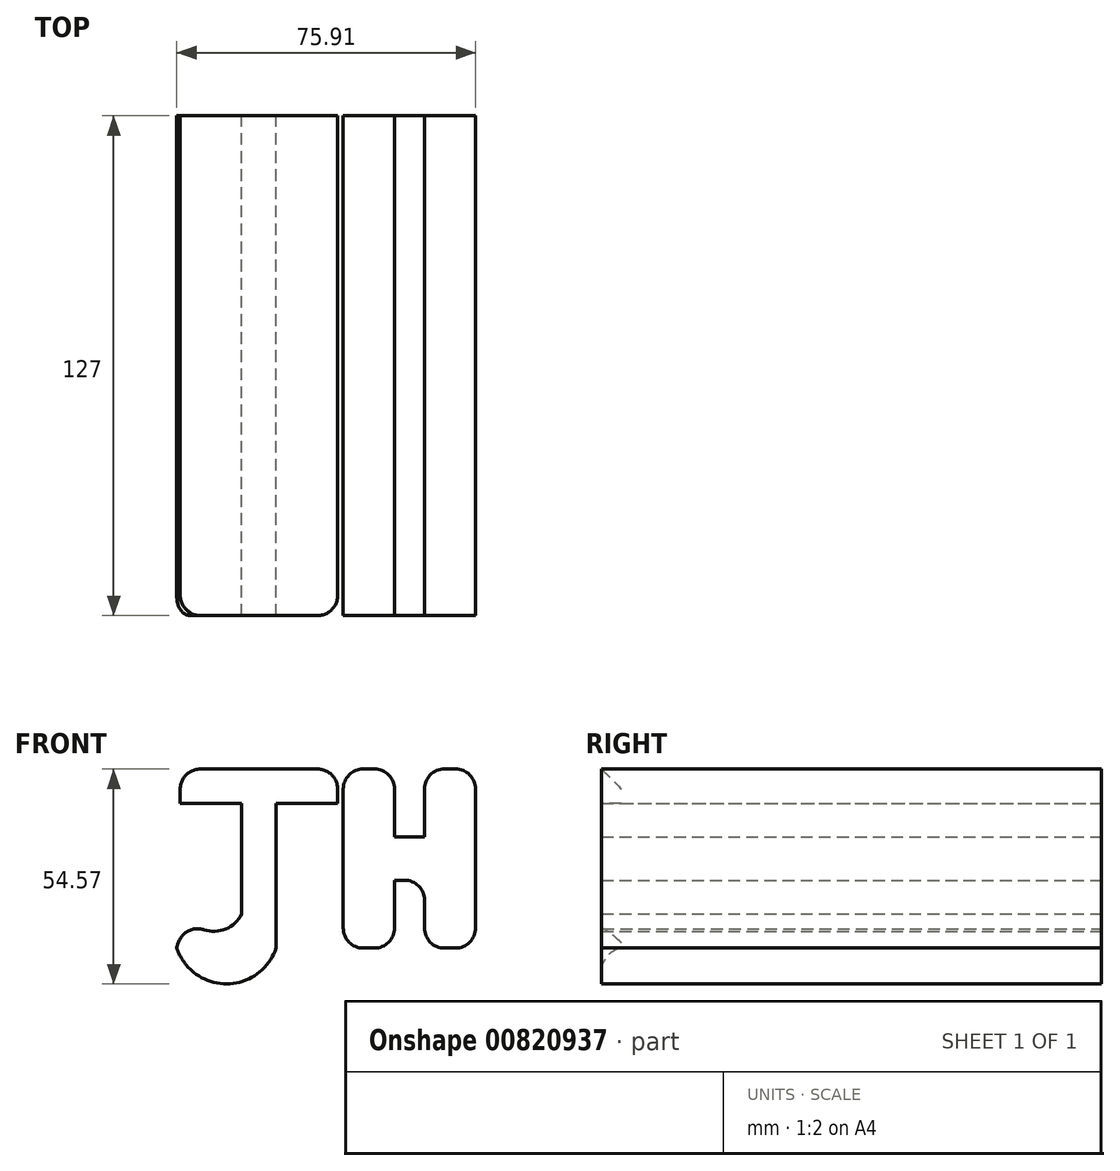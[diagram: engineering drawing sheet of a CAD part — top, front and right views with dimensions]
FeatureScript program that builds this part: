
annotation { "Feature Type Name" : "Feature", "Feature Type Description" : "" }
export const myFeature = defineFeature(function(context is Context, id is Id, definition is map)
    precondition{}
    {
        {
            var Q0;
            Q0=qCreatedBy(makeId("Front.planeOp"),FACE);
            var sketch = newSketch(context, id + "F0", { "sketchPlane" : qUnion([Q0])});
            skLineSegment(sketch, "E0", {"start": v(-75.03, 62.65) * mm, "end": v(-35.03, 62.65) * mm});
            skLineSegment(sketch, "E1", {"start": v(-35.03, 62.65) * mm, "end": v(-35.03, 53.92) * mm});
            skLineSegment(sketch, "E2", {"start": v(-75.03, 62.65) * mm, "end": v(-75.03, 53.92) * mm});
            skLineSegment(sketch, "E3", {"start": v(-75.03, 53.92) * mm, "end": v(-59.4, 53.92) * mm});
            skLineSegment(sketch, "E4", {"start": v(-35.03, 53.92) * mm, "end": v(-50.67, 53.92) * mm});
            skLineSegment(sketch, "E5", {"start": v(-50.67, 53.92) * mm, "end": v(-50.67, 17.16) * mm});
            skLineSegment(sketch, "E6", {"start": v(-33.6, 62.65) * mm, "end": v(-33.6, 17.16) * mm});
            skLineSegment(sketch, "E7", {"start": v(-20.61, 17.16) * mm, "end": v(-33.6, 17.16) * mm});
            skLineSegment(sketch, "E8", {"start": v(-20.61, 17.16) * mm, "end": v(-20.61, 34.42) * mm});
            skLineSegment(sketch, "E9", {"start": v(-20.61, 34.42) * mm, "end": v(-13, 34.42) * mm});
            skLineSegment(sketch, "E10", {"start": v(-13, 17.16) * mm, "end": v(0, 17.16) * mm});
            skLineSegment(sketch, "E11", {"start": v(0, 17.16) * mm, "end": v(-13, 17.16) * mm});
            skLineSegment(sketch, "E12", {"start": v(-13, 34.42) * mm, "end": v(-13, 17.16) * mm});
            skLineSegment(sketch, "E13", {"start": v(0, 17.16) * mm, "end": v(0, 62.65) * mm});
            skLineSegment(sketch, "E14", {"start": v(0, 62.65) * mm, "end": v(-13, 62.65) * mm});
            skLineSegment(sketch, "E15", {"start": v(-13, 62.65) * mm, "end": v(-13, 45.39) * mm});
            skLineSegment(sketch, "E16", {"start": v(-13, 45.39) * mm, "end": v(-20.61, 45.39) * mm});
            skLineSegment(sketch, "E17", {"start": v(-20.61, 45.39) * mm, "end": v(-20.61, 62.65) * mm});
            skLineSegment(sketch, "E18", {"start": v(-20.61, 62.65) * mm, "end": v(-33.6, 62.65) * mm});
            skLineSegment(sketch, "E19", {"start": v(-59.4, 53.92) * mm, "end": v(-59.4, 25.9) * mm});
            skArc(sketch, "E20", {"start": v(-73.41, 25.49) * mm, "mid": v(-66.28, 21.42) * mm, "end": v(-59.4, 25.9) * mm});
            skLineSegment(sketch, "E21", {"start": v(-73.41, 25.49) * mm, "end": v(-75.9, 17.16) * mm});
            skArc(sketch, "E22", {"start": v(-75.9, 17.16) * mm, "mid": v(-63.29, 8.08) * mm, "end": v(-50.67, 17.16) * mm});
            skSolve(sketch);
        }
        {
            var Q0;
            Q0 = qSketchRegion(id + "F0", true);
            extrude(context, id + "F1", {"entities" : qUnion([Q0]), "endBound" : BoundingType.SYMMETRIC, "depth" : 127 * mm, "offsetDistance" : 25.4 * mm});
        }
        {
            var Q0;
            Q0=makeQuery(id+"F1.opExtrude","CAP_EDGE",EDGE,{"disambiguationData":[OSD([sQuery(id+"F0.wireOp",EDGE,"E21")])],"isStart":false});
            var Q1;
            Q1=makeQuery(id+"F1.opExtrude","CAP_EDGE",EDGE,{"disambiguationData":[OSD([sQuery(id+"F0.wireOp",EDGE,"E2")])],"isStart":false});
            var Q2;
            Q2=makeQuery(id+"F1.opExtrude","SWEPT_EDGE",EDGE,{"disambiguationData":[OSD([sQuery(id+"F0.wireOp",EDGE,"E0"),sQuery(id+"F0.wireOp",EDGE,"E2")])]});
            var Q3;
            Q3=makeQuery(id+"F1.opExtrude","SWEPT_EDGE",EDGE,{"disambiguationData":[OSD([sQuery(id+"F0.wireOp",EDGE,"E0"),sQuery(id+"F0.wireOp",EDGE,"E1")])]});
            var Q4;
            Q4=makeQuery(id+"F1.opExtrude","CAP_EDGE",EDGE,{"disambiguationData":[OSD([sQuery(id+"F0.wireOp",EDGE,"E1")])],"isStart":false});
            var Q5;
            Q5=makeQuery(id+"F1.opExtrude","SWEPT_EDGE",EDGE,{"disambiguationData":[OSD([sQuery(id+"F0.wireOp",EDGE,"E20"),sQuery(id+"F0.wireOp",EDGE,"E21")])]});
            var Q6;
            Q6=makeQuery(id+"F1.opExtrude","SWEPT_EDGE",EDGE,{"disambiguationData":[OSD([sQuery(id+"F0.wireOp",EDGE,"E13"),sQuery(id+"F0.wireOp",EDGE,"E14")])]});
            var Q7;
            Q7=makeQuery(id+"F1.opExtrude","SWEPT_EDGE",EDGE,{"disambiguationData":[OSD([sQuery(id+"F0.wireOp",EDGE,"E14"),sQuery(id+"F0.wireOp",EDGE,"E15")])]});
            var Q8;
            Q8=makeQuery(id+"F1.opExtrude","SWEPT_EDGE",EDGE,{"disambiguationData":[OSD([sQuery(id+"F0.wireOp",EDGE,"E17"),sQuery(id+"F0.wireOp",EDGE,"E18")])]});
            var Q9;
            Q9=makeQuery(id+"F1.opExtrude","SWEPT_EDGE",EDGE,{"disambiguationData":[OSD([sQuery(id+"F0.wireOp",EDGE,"E6"),sQuery(id+"F0.wireOp",EDGE,"E18")])]});
            var Q10;
            Q10=makeQuery(id+"F1.opExtrude","SWEPT_EDGE",EDGE,{"disambiguationData":[OSD([sQuery(id+"F0.wireOp",EDGE,"E11"),sQuery(id+"F0.wireOp",EDGE,"E13")])]});
            var Q11;
            Q11=makeQuery(id+"F1.opExtrude","SWEPT_EDGE",EDGE,{"disambiguationData":[OSD([sQuery(id+"F0.wireOp",EDGE,"E7"),sQuery(id+"F0.wireOp",EDGE,"E8")])]});
            var Q12;
            Q12=makeQuery(id+"F1.opExtrude","SWEPT_EDGE",EDGE,{"disambiguationData":[OSD([sQuery(id+"F0.wireOp",EDGE,"E6"),sQuery(id+"F0.wireOp",EDGE,"E7")])]});
            var Q13;
            Q13=makeQuery(id+"F1.opExtrude","SWEPT_EDGE",EDGE,{"disambiguationData":[OSD([sQuery(id+"F0.wireOp",EDGE,"E11"),sQuery(id+"F0.wireOp",EDGE,"E12")])]});
            fillet(context, id + "F2", {"entities" : qUnion([Q0, Q1, Q2, Q3, Q4, Q5, Q6, Q7, Q8, Q9, Q10, Q11, Q12, Q13]), "radius" : 5.08 * mm, "tangentPropagation" : true, "allowEdgeOverflow" : false});
        }
    });
